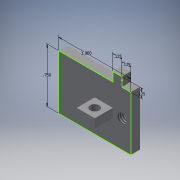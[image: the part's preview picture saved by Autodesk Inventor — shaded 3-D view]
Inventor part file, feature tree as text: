
AUTODESK INVENTOR PART (.ipt)
format: ipt  version: 2016 (Build 200138000, 138)  size: 140,288 bytes
history: native  units: in
note: dims shown in document units (in); Inventor stores cm internally (conversion verified against a paired STEP export)
features: sketch x6, hole x3, projected_geometry x3, extrude x2, thicken_offset x1
ambient origin geometry x8: Origin, YZ Plane, XZ Plane, XY Plane, X Axis, Y Axis, Z Axis, Center Point
bodies: Solid1 (feature_tree)
feature tree (15):
  extrude  "Extrusion1"  Depth=1.0in
  extrude  "Extrusion2"  Depth=0.125in
  hole  "Hole1"  [1 undecoded]
  hole  "Hole2"  [1 undecoded]
  hole  "Hole3"  [1 undecoded]
  sketch  "Sketch6"  dims[d15=0.06in d16=0.75in d17=0.375in d18=0.25in d19=0.5635in d20=1.0in d21=0.8108in d22=0.125in d23=0.125in d24=0.75in d25=0.375in d26=0.25in d27=0.5635in d28=1.0in d29=0.8108in d30=0.13in d31=0.75in d32=0.375in d33=0.25in d34=0.5635in d35=1.0in d36=0.8108in d37=0.125in d38=0.063in d39=0.57in d40=0.57in]
  thicken_offset  "Thicken1"
  sketch  "Sketch1"  dims[d0=0.75in d2=1.0in]
  sketch  "Sketch2"  dims[d3=0.125in d4=0.125in]
  sketch  "Sketch3"  dims[d5=0.125in d6=0.0in d7=0.125in]
  projected_geometry  "Projected Loop1"
  sketch  "Sketch4"  dims[d10=0.25in d11=0.3125in]
  projected_geometry  "Projected Loop2"
  sketch  "Sketch5"  dims[d12=0.25in d13=0.25in d14=0.0in]
  projected_geometry  "Projected Loop3"
note: 3 required parameter values undecoded (feature->parameter linkage not recoverable at this tier; creation-order binding heuristic only, values carry confidence <= 0.55)
